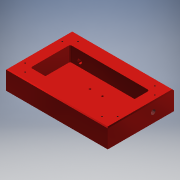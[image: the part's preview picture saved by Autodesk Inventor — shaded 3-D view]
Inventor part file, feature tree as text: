
AUTODESK INVENTOR PART (.ipt)
format: ipt  version: 2019.4 (Build 234330000, 330)  size: 212,480 bytes
history: native  units: mm
features: sketch x6, hole x4, extrude x2, fillet x1, chamfer x1
ambient origin geometry x8: Origin, YZ Plane, XZ Plane, XY Plane, X Axis, Y Axis, Z Axis, Center Point
bodies: Volumenkörper1 (feature_tree)
feature tree (14):
  extrude  "Extrusion1"  Depth=160.0mm
  extrude  "Extrusion2"  Depth=192.0mm
  fillet  "Rundung1"  Radius=96.0mm
  chamfer  "Fase1"  Distance=36.0mm
  sketch  "Skizze4"  dims[d10=4.0mm d11=2.0mm d12=2.0mm d13=45.0deg]
  hole  "Bohrung3"  [1 undecoded]
  hole  "Bohrung7"  [1 undecoded]
  hole  "Hole8"  [1 undecoded]
  hole  "Hole9"  [1 undecoded]
  sketch  "Skizze1"  dims[d0=246.0mm d2=160.0mm]
  sketch  "Skizze2"  dims[d3=46.0mm d4=0.0mm d5=192.0mm d7=96.0mm d8=36.0mm d9=0.0mm]
  sketch  "Sketch10"  dims[d14=8.0mm d15=30.0mm]
  sketch  "Sketch11"  dims[d16=30.0mm d17=8.0mm]
  sketch  "Sketch13"  dims[d18=8.0mm d19=30.0mm d20=8.0mm d21=30.0mm d22=30.0mm d23=8.0mm d24=8.0mm d25=30.0mm d26=8.0mm d27=30.0mm d28=30.0mm d29=8.0mm d30=4.0mm d31=4.0mm d32=4.0mm d33=4.0mm d34=4.0mm d35=4.0mm d36=4.0mm d37=4.0mm d92=23.0mm d93=110.0mm d94=10.719mm d95=10.02mm d96=6.0mm d97=10.0mm d98=90.0deg d99=17.076mm d100=20.594885mm d153=35.0mm d154=35.0mm d155=11.0mm d156=16.0mm d157=30.0mm d158=11.0mm d159=16.0mm d160=30.0mm d161=30.0mm d162=16.0mm d163=11.0mm d164=35.0mm d165=11.0mm d166=35.0mm d167=16.0mm d168=30.0mm d169=3.242mm d170=6.0mm d171=8.0mm d172=4.6mm d173=14.3117mm d174=20.0mm d175=20.594885mm d176=0.624793mm d177=10.732mm d182=22.0mm d183=50.0mm d184=10.719mm d185=8.608mm d186=0.624793mm d187=10.821mm d188=19.05mm d189=4.775mm d190=90.0deg d191=15.664mm d192=20.594885mm d199=4.5mm d200=8.608mm d201=12.6mm d202=2.0mm d203=90.0deg d204=8.0mm d205=20.594885mm d206=15.0mm d207=15.0mm d208=20.0mm d210=30.0mm d211=20.0mm d213=30.0mm]
note: 4 required parameter values undecoded (feature->parameter linkage not recoverable at this tier; creation-order binding heuristic only, values carry confidence <= 0.55)
